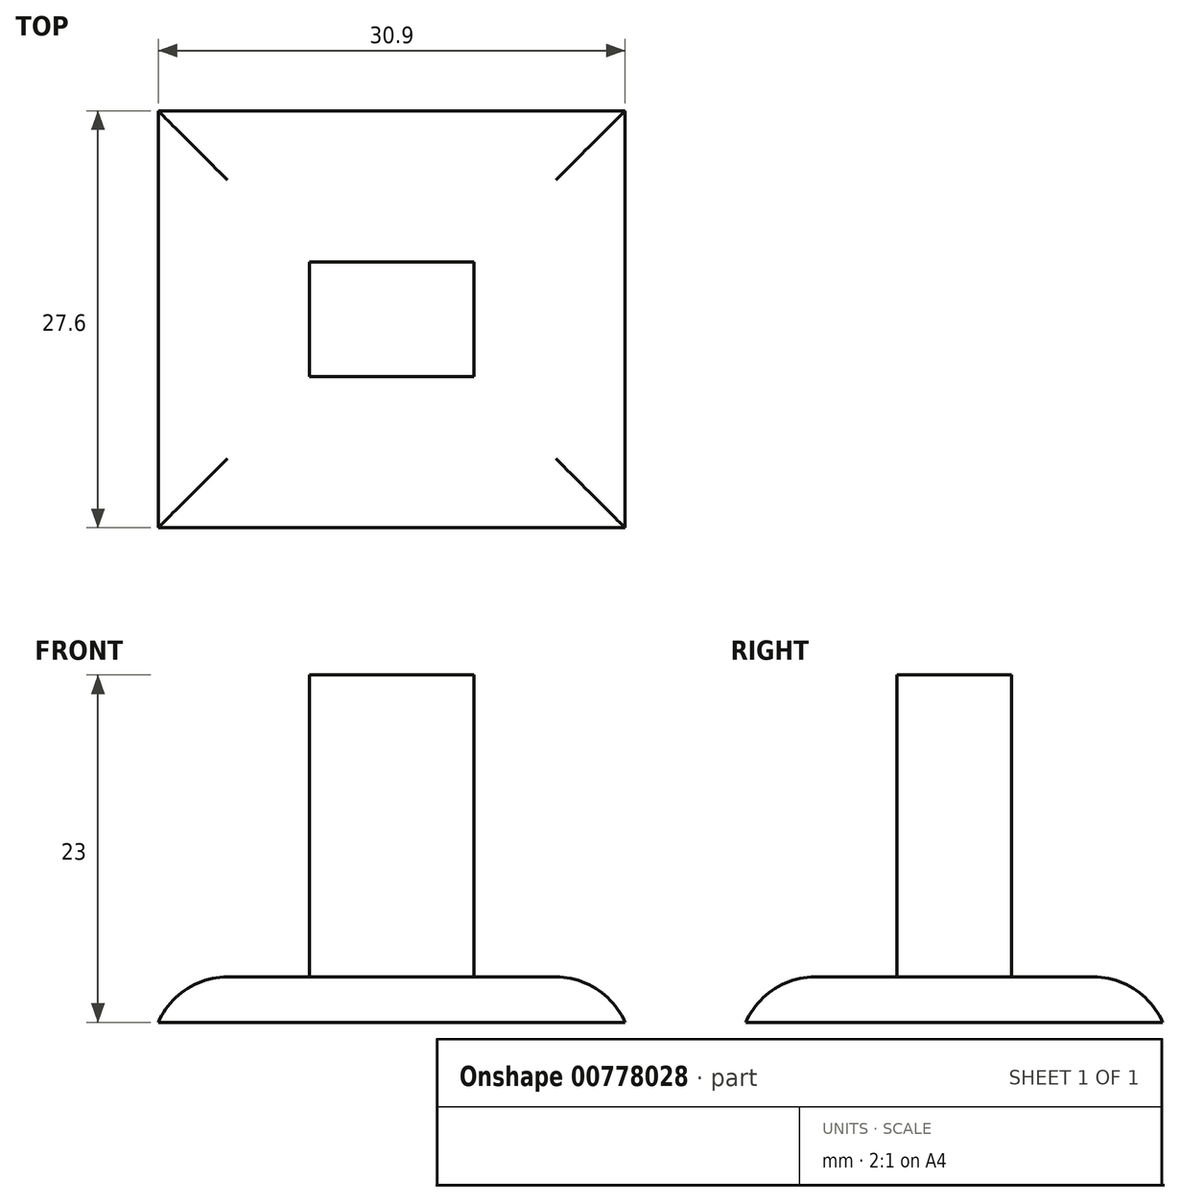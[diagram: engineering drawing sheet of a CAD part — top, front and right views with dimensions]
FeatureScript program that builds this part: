
annotation { "Feature Type Name" : "Feature", "Feature Type Description" : "" }
export const myFeature = defineFeature(function(context is Context, id is Id, definition is map)
    precondition{}
    {
        {
            var Q0;
            Q0=qCreatedBy(makeId("Top.planeOp"),FACE);
            var sketch = newSketch(context, id + "F0", { "sketchPlane" : qUnion([Q0])});
            skLineSegment(sketch, "E0.bottom", {"start": v(-3.93, 13.9) * mm, "end": v(6.97, 13.9) * mm});
            skLineSegment(sketch, "E0.top", {"start": v(-3.93, 6.3) * mm, "end": v(6.97, 6.3) * mm});
            skLineSegment(sketch, "E0.left", {"start": v(-3.93, 13.9) * mm, "end": v(-3.93, 6.3) * mm});
            skLineSegment(sketch, "E0.right", {"start": v(6.97, 13.9) * mm, "end": v(6.97, 6.3) * mm});
            skSolve(sketch);
        }
        {
            var Q0;
            Q0=makeQuery(id+"F0.imprint","IMPRINT",FACE,{"disambiguationData":[TD([[makeQuery(id+"F0.imprint","IMPRINT",EDGE,{"derivedFrom":sQuery(id+"F0.wireOp",EDGE,"E0.bottom")}),-1.0]])]});
            extrude(context, id + "F1", {"entities" : qUnion([Q0]), "depth" : 20 * mm, "offsetDistance" : 25 * mm});
        }
        {
            var Q0;
            Q0=makeQuery(id+"F1.opExtrude","CAP_FACE",FACE,{"disambiguationData":[OSD([sQuery(id+"F0.wireOp",EDGE,"E0.bottom"),sQuery(id+"F0.wireOp",EDGE,"E0.top"),sQuery(id+"F0.wireOp",EDGE,"E0.left"),sQuery(id+"F0.wireOp",EDGE,"E0.right")])],"isStart":true});
            var sketch = newSketch(context, id + "F2", { "sketchPlane" : qUnion([Q0])});
            skLineSegment(sketch, "E1.0", {"start": v(-13.93, 3.7) * mm, "end": v(16.97, 3.7) * mm});
            skLineSegment(sketch, "E1.1", {"start": v(-13.93, -23.9) * mm, "end": v(-13.93, 3.7) * mm});
            skLineSegment(sketch, "E1.2", {"start": v(-13.93, -23.9) * mm, "end": v(16.97, -23.9) * mm});
            skLineSegment(sketch, "E1.3", {"start": v(16.97, -23.9) * mm, "end": v(16.97, 3.7) * mm});
            skSolve(sketch);
        }
        {
            var Q0;
            Q0=makeQuery(id+"F2.imprint","IMPRINT",FACE,{"disambiguationData":[TD([[makeQuery(id+"F2.imprint","IMPRINT",EDGE,{"derivedFrom":sQuery(id+"F2.wireOp",EDGE,"E1.0")}),-1.0]])]});
            var Q1;
            Q1=makeQuery(id+"F2.imprint","IMPRINT",FACE,{"disambiguationData":[TD([[makeQuery(id+"F2.imprint","IMPRINT",EDGE,{"derivedFrom":makeQuery(id+"F1.opExtrude","CAP_EDGE",EDGE,{"disambiguationData":[OSD([sQuery(id+"F0.wireOp",EDGE,"E0.bottom")])],"isStart":true})}),1.0]])]});
            extrude(context, id + "F3", {"entities" : qUnion([Q0, Q1]), "operationType" : NewBodyOperationType.ADD, "depth" : 3 * mm, "offsetDistance" : 25 * mm});
        }
        {
            var Q0;
            Q0=makeQuery(id+"F3.opExtrude","CAP_EDGE",EDGE,{"disambiguationData":[OSD([sQuery(id+"F2.wireOp",EDGE,"E1.1")])],"isStart":true});
            var Q1;
            Q1=makeQuery(id+"F3.opExtrude","CAP_EDGE",EDGE,{"disambiguationData":[OSD([sQuery(id+"F2.wireOp",EDGE,"E1.0")])],"isStart":true});
            var Q2;
            Q2=makeQuery(id+"F3.opExtrude","CAP_EDGE",EDGE,{"disambiguationData":[OSD([sQuery(id+"F2.wireOp",EDGE,"E1.3")])],"isStart":true});
            var Q3;
            Q3=makeQuery(id+"F3.opExtrude","CAP_EDGE",EDGE,{"disambiguationData":[OSD([sQuery(id+"F2.wireOp",EDGE,"E1.2")])],"isStart":true});
            fillet(context, id + "F4", {"entities" : qUnion([Q0, Q1, Q2, Q3]), "radius" : 5 * mm, "tangentPropagation" : true, "allowEdgeOverflow" : false});
        }
    });
